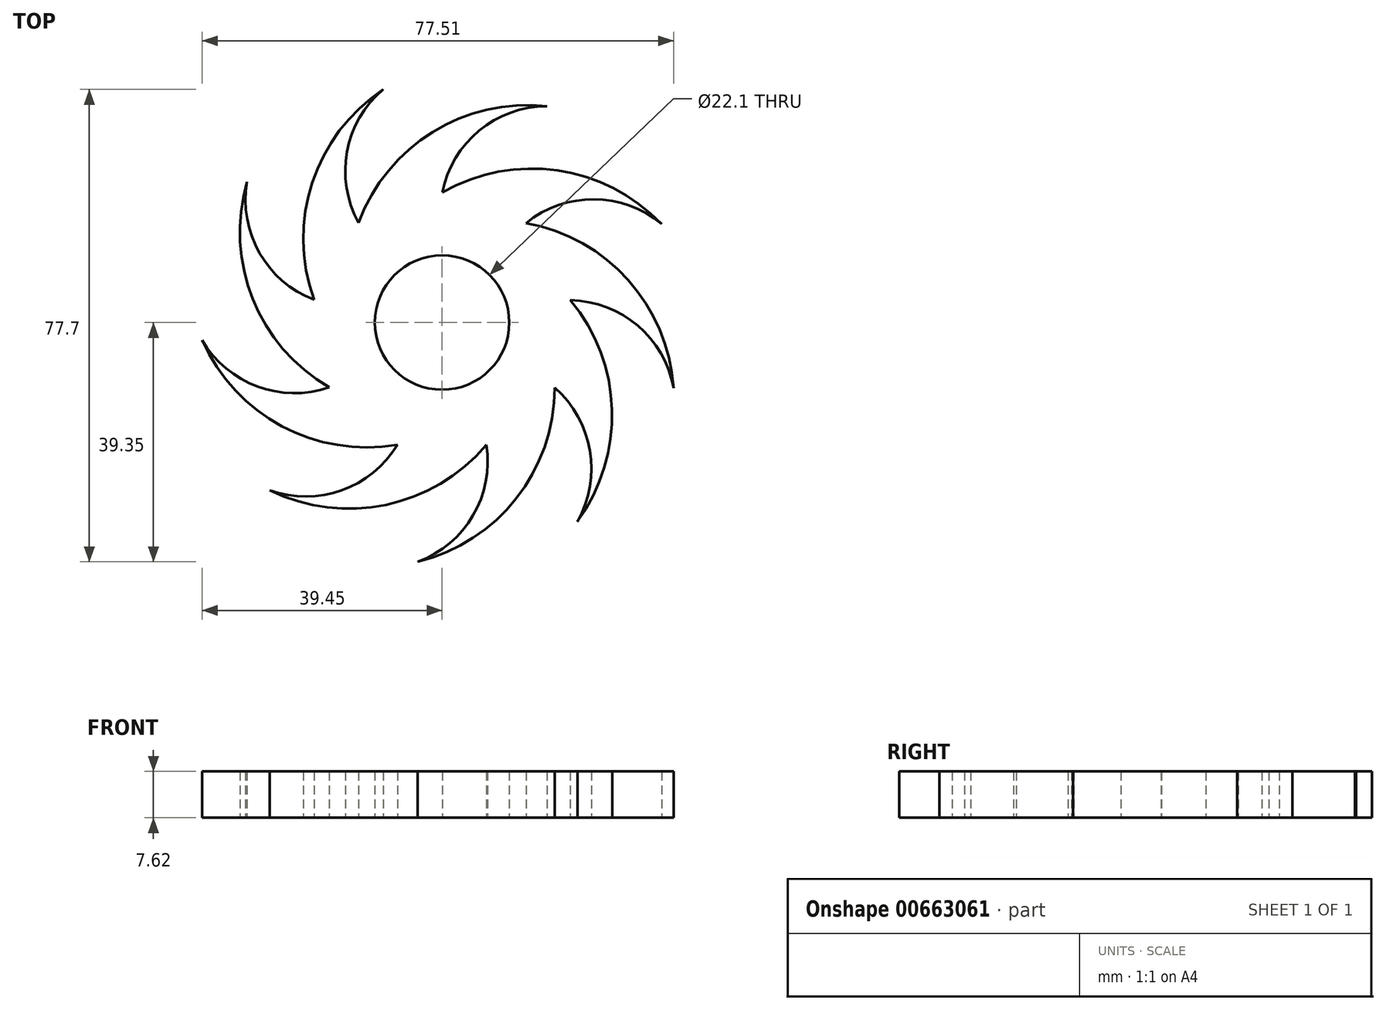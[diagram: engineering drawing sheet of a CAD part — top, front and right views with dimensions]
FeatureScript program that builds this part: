
annotation { "Feature Type Name" : "Feature", "Feature Type Description" : "" }
export const myFeature = defineFeature(function(context is Context, id is Id, definition is map)
    precondition{}
    {
        {
            var Q0;
            Q0=qCreatedBy(makeId("Top.planeOp"),FACE);
            var sketch = newSketch(context, id + "F0", { "sketchPlane" : qUnion([Q0])});
            skCircle(sketch, "E0", {"center": v(0, 0) * mm, "radius": 11.05 * mm});
            skArc(sketch, "E1", {"start": v(17.22, 35.61) * mm, "mid": v(-1.56, 31.35) * mm, "end": v(-13.73, 16.42) * mm});
            skArc(sketch, "E2", {"start": v(17.22, 35.61) * mm, "mid": v(6.09, 31.58) * mm, "end": v(0.04, 21.4) * mm});
            skArc(sketch, "E3.1.0", {"start": v(-9.7, 38.35) * mm, "mid": v(-15.63, 28.1) * mm, "end": v(-13.73, 16.42) * mm});
            skArc(sketch, "E3.1.1", {"start": v(-9.7, 38.35) * mm, "mid": v(-21.35, 23.01) * mm, "end": v(-21.07, 3.76) * mm});
            skArc(sketch, "E3.2.0", {"start": v(-32.08, 23.14) * mm, "mid": v(-30.04, 11.48) * mm, "end": v(-21.07, 3.76) * mm});
            skArc(sketch, "E3.2.1", {"start": v(-32.08, 23.14) * mm, "mid": v(-31.15, 3.9) * mm, "end": v(-18.55, -10.67) * mm});
            skArc(sketch, "E3.3.0", {"start": v(-39.45, -2.9) * mm, "mid": v(-30.4, -10.52) * mm, "end": v(-18.55, -10.67) * mm});
            skArc(sketch, "E3.3.1", {"start": v(-39.45, -2.9) * mm, "mid": v(-26.37, -17.03) * mm, "end": v(-7.36, -20.1) * mm});
            skArc(sketch, "E4.3.4.0", {"start": v(-28.36, -27.57) * mm, "mid": v(-16.52, -27.6) * mm, "end": v(-7.36, -20.1) * mm});
            skArc(sketch, "E4.4.4.0", {"start": v(-28.36, -27.57) * mm, "mid": v(-9.26, -30) * mm, "end": v(7.28, -20.12) * mm});
            skArc(sketch, "E4.3.5.0", {"start": v(-4, -39.35) * mm, "mid": v(5.08, -31.76) * mm, "end": v(7.28, -20.12) * mm});
            skArc(sketch, "E4.4.5.0", {"start": v(-4, -39.35) * mm, "mid": v(12.19, -28.93) * mm, "end": v(18.51, -10.73) * mm});
            skArc(sketch, "E5.3.6.0", {"start": v(22.23, -32.72) * mm, "mid": v(24.3, -21.06) * mm, "end": v(18.51, -10.73) * mm});
            skArc(sketch, "E5.4.6.0", {"start": v(22.23, -32.72) * mm, "mid": v(27.93, -14.32) * mm, "end": v(21.08, 3.68) * mm});
            skArc(sketch, "E5.3.7.0", {"start": v(38.06, -10.77) * mm, "mid": v(32.16, -0.51) * mm, "end": v(21.08, 3.68) * mm});
            skArc(sketch, "E5.4.7.0", {"start": v(38.06, -10.77) * mm, "mid": v(30.6, 6.98) * mm, "end": v(13.79, 16.37) * mm});
            skArc(sketch, "E5.3.8.0", {"start": v(36.08, 16.21) * mm, "mid": v(24.96, 20.28) * mm, "end": v(13.79, 16.37) * mm});
            skArc(sketch, "E5.4.8.0", {"start": v(36.08, 16.21) * mm, "mid": v(18.96, 25.02) * mm, "end": v(0.04, 21.4) * mm});
            skPoint(sketch, "E6.orphan", {"position": v(-11.39, 9.56) * mm});
            skPoint(sketch, "E7.orphan", {"position": v(-9.56, 11.39) * mm});
            skPoint(sketch, "E8.orphan", {"position": v(7.43, 12.87) * mm});
            skPoint(sketch, "E9.trimOffspring.end.orphan", {"position": v(-14.87, 0) * mm});
            skPoint(sketch, "E10.orphan", {"position": v(-5.08, -13.97) * mm});
            skPoint(sketch, "E11.trimOffspring.end.orphan", {"position": v(0, 14.87) * mm});
            skSolve(sketch);
        }
        {
            var Q0;
            Q0 = qSketchRegion(id + "F0", true);
            extrude(context, id + "F1", {"entities" : qUnion([Q0]), "depth" : 7.62 * mm, "offsetDistance" : 25.4 * mm});
        }
    });
